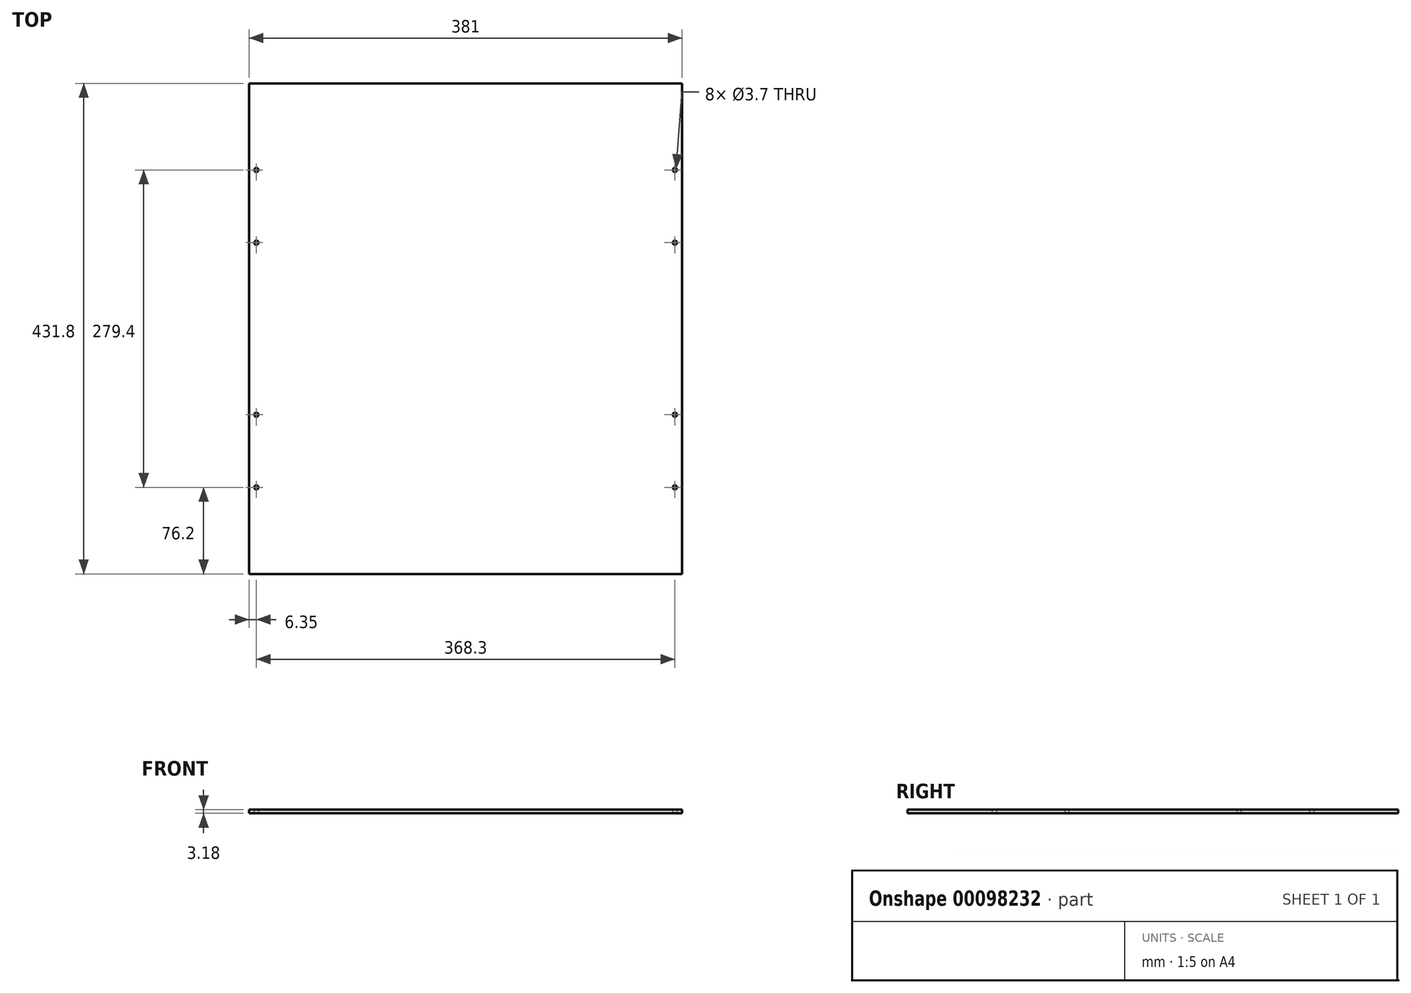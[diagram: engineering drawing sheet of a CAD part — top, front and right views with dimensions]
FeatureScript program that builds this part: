
annotation { "Feature Type Name" : "Feature", "Feature Type Description" : "" }
export const myFeature = defineFeature(function(context is Context, id is Id, definition is map)
    precondition{}
    {
        {
            var Q0;
            Q0=qCreatedBy(makeId("Top.planeOp"),FACE);
            var sketch = newSketch(context, id + "F0", { "sketchPlane" : qUnion([Q0])});
            skLineSegment(sketch, "E0.bottom", {"start": v(190.5, 215.9) * mm, "end": v(-190.5, 215.9) * mm});
            skLineSegment(sketch, "E0.top", {"start": v(190.5, -215.9) * mm, "end": v(-190.5, -215.9) * mm});
            skLineSegment(sketch, "E0.left", {"start": v(190.5, 215.9) * mm, "end": v(190.5, -215.9) * mm});
            skLineSegment(sketch, "E0.right", {"start": v(-190.5, 215.9) * mm, "end": v(-190.5, -215.9) * mm});
            skPoint(sketch, "E0.middle", {"position": v(0, 0) * mm});
            skPoint(sketch, "E1", {"position": v(-184.15, 139.7) * mm});
            skPoint(sketch, "E2", {"position": v(-184.15, 75.7) * mm});
            skPoint(sketch, "E3", {"position": v(-184.15, -75.7) * mm});
            skPoint(sketch, "E4", {"position": v(-184.15, -139.7) * mm});
            skPoint(sketch, "E5", {"position": v(184.15, -75.7) * mm});
            skPoint(sketch, "E6", {"position": v(184.15, -139.7) * mm});
            skPoint(sketch, "E7", {"position": v(184.15, 139.7) * mm});
            skPoint(sketch, "E8", {"position": v(184.15, 75.7) * mm});
            skCircle(sketch, "E9", {"center": v(-184.15, 139.7) * mm, "radius": 1.85 * mm});
            skCircle(sketch, "E10", {"center": v(-184.15, 75.7) * mm, "radius": 1.85 * mm});
            skCircle(sketch, "E11", {"center": v(-184.15, -75.7) * mm, "radius": 1.85 * mm});
            skCircle(sketch, "E12", {"center": v(-184.15, -139.7) * mm, "radius": 1.85 * mm});
            skCircle(sketch, "E13", {"center": v(184.15, -75.7) * mm, "radius": 1.85 * mm});
            skCircle(sketch, "E14", {"center": v(184.15, -139.7) * mm, "radius": 1.85 * mm});
            skCircle(sketch, "E15", {"center": v(184.15, 139.7) * mm, "radius": 1.85 * mm});
            skCircle(sketch, "E16", {"center": v(184.15, 75.7) * mm, "radius": 1.85 * mm});
            skSolve(sketch);
        }
        {
            var Q0;
            Q0=makeQuery(id+"F0.imprint","IMPRINT",FACE,{"disambiguationData":[TD([[makeQuery(id+"F0.imprint","IMPRINT",EDGE,{"derivedFrom":sQuery(id+"F0.wireOp",EDGE,"E0.top")}),-1.0]])]});
            extrude(context, id + "F1", {"entities" : qUnion([Q0]), "depth" : 3.17 * mm});
        }
    });
